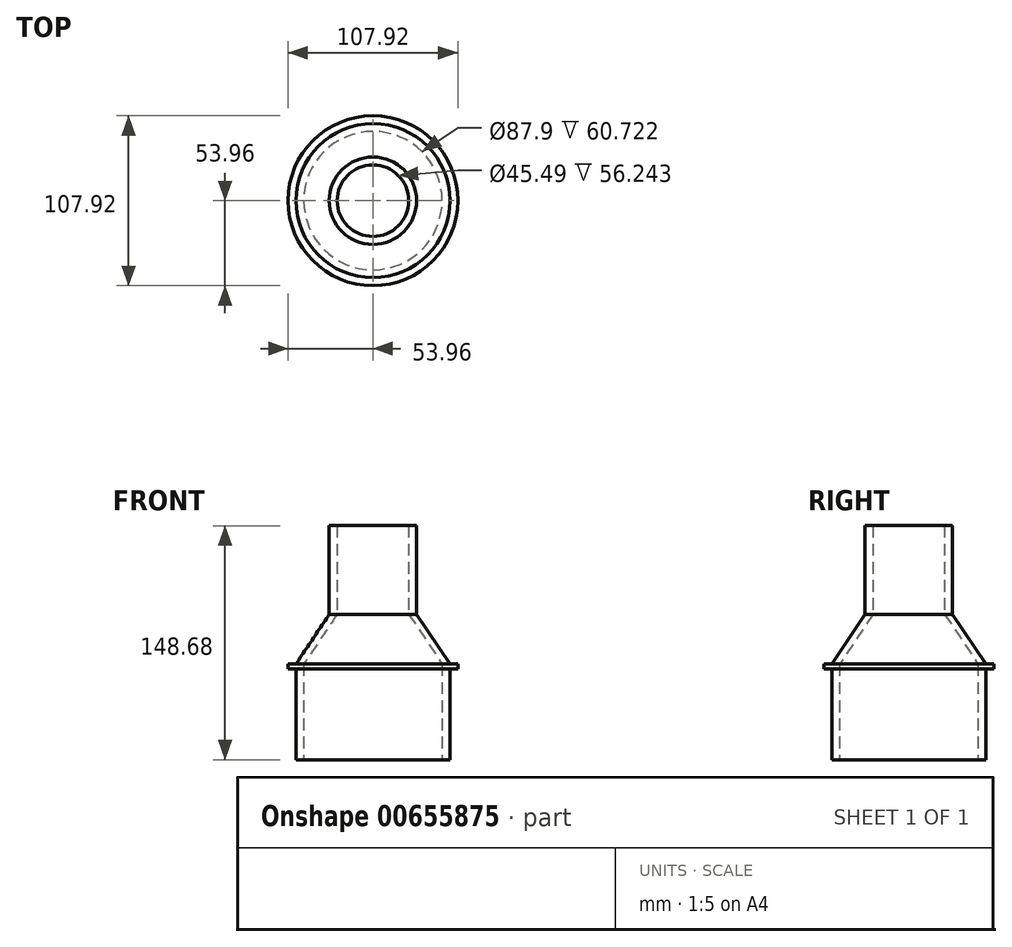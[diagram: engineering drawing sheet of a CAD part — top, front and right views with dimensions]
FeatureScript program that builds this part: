
annotation { "Feature Type Name" : "Feature", "Feature Type Description" : "" }
export const myFeature = defineFeature(function(context is Context, id is Id, definition is map)
    precondition{}
    {
        {
            var Q0;
            Q0=qCreatedBy(makeId("Front.planeOp"),FACE);
            var sketch = newSketch(context, id + "F0", { "sketchPlane" : qUnion([Q0])});
            skLineSegment(sketch, "E0", {"start": v(-27.74, 113.51) * mm, "end": v(-27.74, 57.17) * mm});
            skLineSegment(sketch, "E1", {"start": v(-48.95, -35.27) * mm, "end": v(-43.95, -35.27) * mm});
            skLineSegment(sketch, "E2", {"start": v(-43.95, -35.27) * mm, "end": v(-43.95, 25.45) * mm});
            skLineSegment(sketch, "E3", {"start": v(-43.95, 25.45) * mm, "end": v(-22.74, 57.17) * mm});
            skLineSegment(sketch, "E4", {"start": v(-22.74, 57.17) * mm, "end": v(-22.74, 113.41) * mm});
            skLineSegment(sketch, "E5", {"start": v(-22.74, 113.41) * mm, "end": v(-27.74, 113.41) * mm});
            skLineSegment(sketch, "E6", {"start": v(0, -40.04) * mm, "end": v(0, 115.42) * mm});
            skLineSegment(sketch, "E7", {"start": v(-27.74, 57.17) * mm, "end": v(-48.9, 25.53) * mm});
            skLineSegment(sketch, "E8", {"start": v(-48.9, 25.53) * mm, "end": v(-48.95, -35.27) * mm});
            skLineSegment(sketch, "E9", {"start": v(-48.9, 25.53) * mm, "end": v(-53.96, 25.53) * mm});
            skLineSegment(sketch, "E10", {"start": v(-53.96, 25.53) * mm, "end": v(-53.96, 22.4) * mm});
            skLineSegment(sketch, "E11", {"start": v(-53.96, 22.4) * mm, "end": v(-48.9, 22.4) * mm});
            skSolve(sketch);
        }
        {
            var Q0;
            {var subQ0=sQuery(id+"F0.wireOp",EDGE,"E1");Q0=makeQuery(id+"F0.imprint","IMPRINT",FACE,{"disambiguationData":[TD([[makeQuery(id+"F0.imprint","IMPRINT",EDGE,{"derivedFrom":subQ0}),1.0]])]});}
            var Q1;
            {var subQ0=sQuery(id+"F0.wireOp",EDGE,"E9");Q1=makeQuery(id+"F0.imprint","IMPRINT",FACE,{"disambiguationData":[TD([[makeQuery(id+"F0.imprint","IMPRINT",EDGE,{"derivedFrom":subQ0}),1.0]])]});}
            var Q2;
            Q2=sQuery(id+"F0.wireOp",EDGE,"E6");
            revolve(context, id + "F1", {"entities" : qUnion([Q0, Q1]), "axis" : qUnion([Q2]), "revolveType" : RevolveType.FULL});
        }
    });
